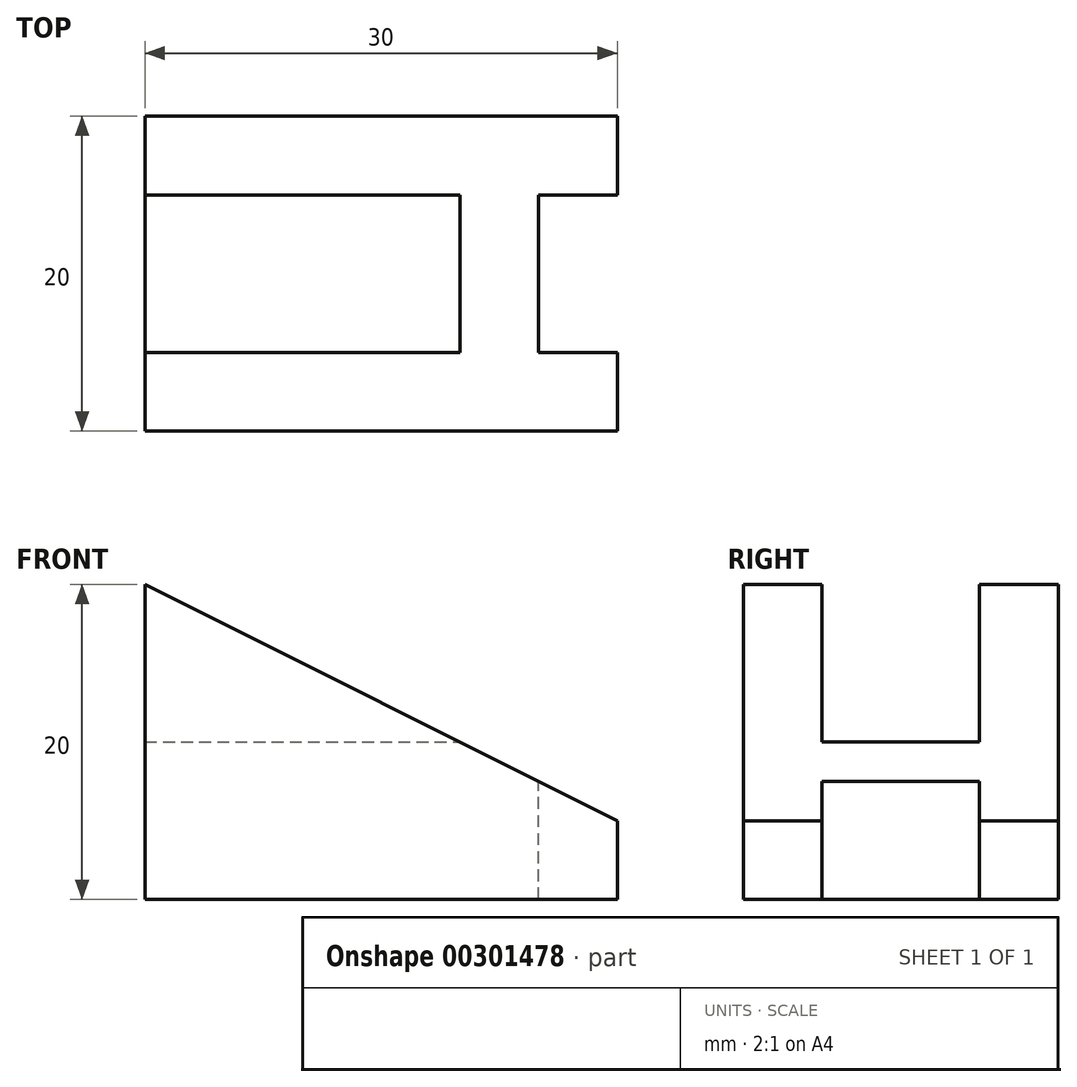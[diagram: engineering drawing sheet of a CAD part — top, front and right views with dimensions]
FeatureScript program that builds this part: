
annotation { "Feature Type Name" : "Feature", "Feature Type Description" : "" }
export const myFeature = defineFeature(function(context is Context, id is Id, definition is map)
    precondition{}
    {
        {
            var Q0;
            Q0=qCreatedBy(makeId("Front.planeOp"),FACE);
            var sketch = newSketch(context, id + "F0", { "sketchPlane" : qUnion([Q0])});
            skLineSegment(sketch, "E0", {"start": v(0, 0) * mm, "end": v(30, 0) * mm});
            skLineSegment(sketch, "E1", {"start": v(30, 0) * mm, "end": v(30, 5) * mm});
            skLineSegment(sketch, "E2", {"start": v(0, 0) * mm, "end": v(0, 20) * mm});
            skLineSegment(sketch, "E3", {"start": v(0, 20) * mm, "end": v(30, 5) * mm});
            skLineSegment(sketch, "E4", {"start": v(0, 10) * mm, "end": v(20, 10) * mm});
            skLineSegment(sketch, "E5", {"start": v(25, 0) * mm, "end": v(25, 7.5) * mm});
            skSolve(sketch);
        }
        {
            var Q0;
            {var subQ3=sQuery(id+"F0.wireOp",EDGE,"E4");Q0=makeQuery(id+"F0.imprint","IMPRINT",FACE,{"disambiguationData":[TD([[makeQuery(id+"F0.imprint","IMPRINT",EDGE,{"derivedFrom":subQ3}),1.0]])]});}
            var Q1;
            {var subQ0=sQuery(id+"F0.wireOp",EDGE,"E4");Q1=makeQuery(id+"F0.imprint","IMPRINT",FACE,{"disambiguationData":[TD([[makeQuery(id+"F0.imprint","IMPRINT",EDGE,{"derivedFrom":subQ0}),-1.0]])]});}
            var Q2;
            {var subQ0=sQuery(id+"F0.wireOp",EDGE,"E1");Q2=makeQuery(id+"F0.imprint","IMPRINT",FACE,{"disambiguationData":[TD([[makeQuery(id+"F0.imprint","IMPRINT",EDGE,{"derivedFrom":subQ0}),1.0]])]});}
            extrude(context, id + "F1", {"entities" : qUnion([Q0, Q1, Q2]), "endBound" : BoundingType.SYMMETRIC, "depth" : 20 * mm});
        }
        {
            var Q0;
            {var subQ3=sQuery(id+"F0.wireOp",EDGE,"E4");Q0=makeQuery(id+"F0.imprint","IMPRINT",FACE,{"disambiguationData":[TD([[makeQuery(id+"F0.imprint","IMPRINT",EDGE,{"derivedFrom":subQ3}),1.0]])]});}
            var Q1;
            {var subQ0=sQuery(id+"F0.wireOp",EDGE,"E1");Q1=makeQuery(id+"F0.imprint","IMPRINT",FACE,{"disambiguationData":[TD([[makeQuery(id+"F0.imprint","IMPRINT",EDGE,{"derivedFrom":subQ0}),1.0]])]});}
            extrude(context, id + "F2", {"entities" : qUnion([Q0, Q1]), "operationType" : NewBodyOperationType.REMOVE, "endBound" : BoundingType.SYMMETRIC, "oppositeDirection" : true, "depth" : 10 * mm});
        }
    });
